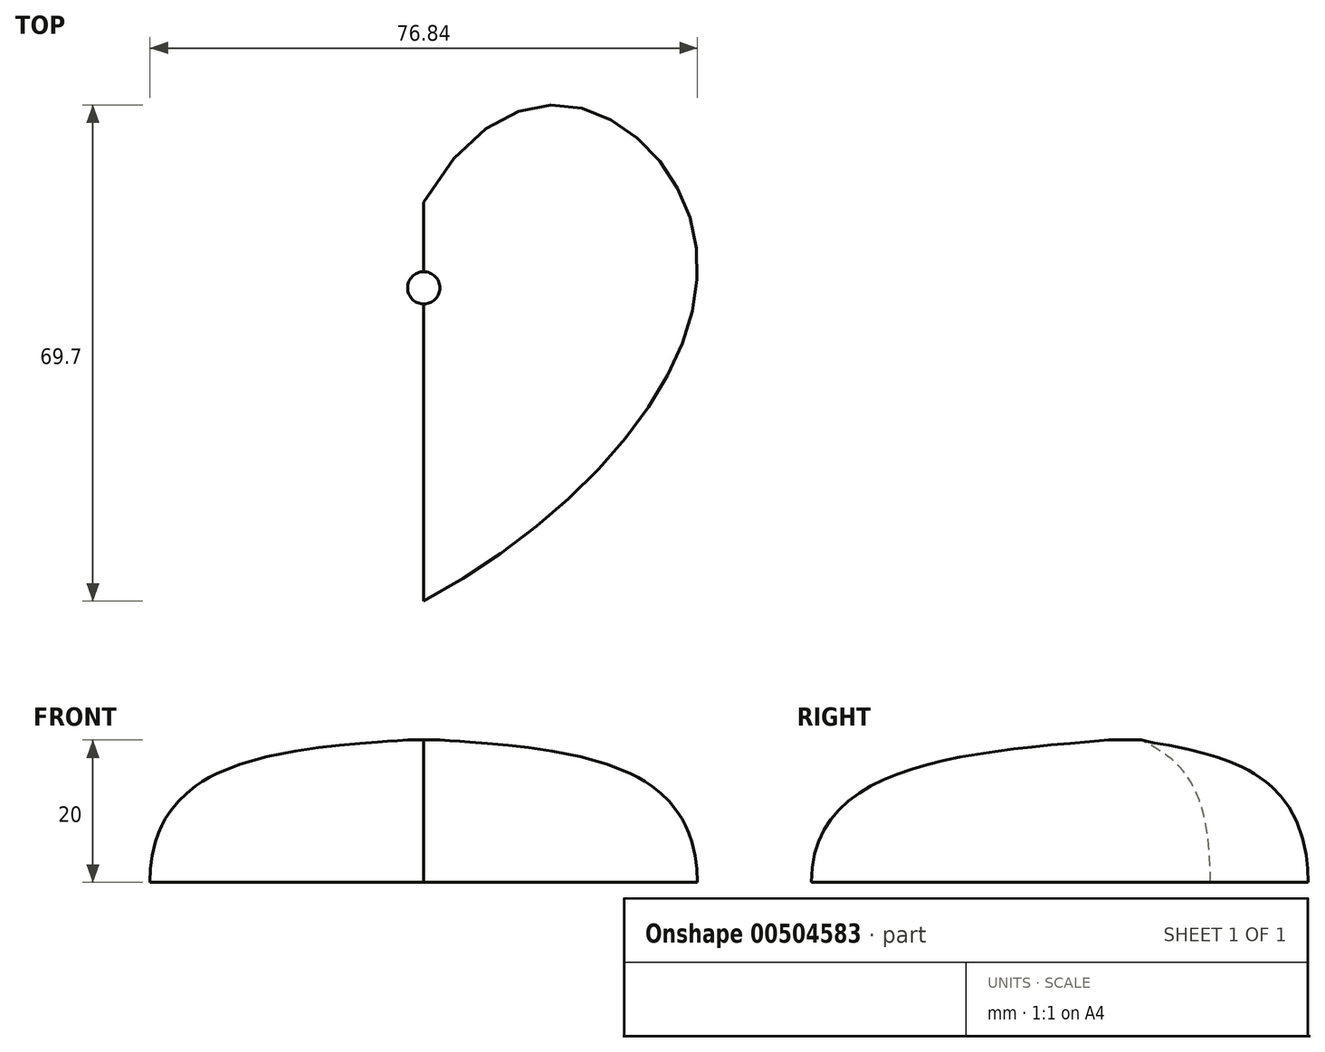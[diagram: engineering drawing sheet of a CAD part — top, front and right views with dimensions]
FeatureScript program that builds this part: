
annotation { "Feature Type Name" : "Feature", "Feature Type Description" : "" }
export const myFeature = defineFeature(function(context is Context, id is Id, definition is map)
    precondition{}
    {
        {
            var Q0;
            Q0=qCreatedBy(makeId("Top.planeOp"),FACE);
            var sketch = newSketch(context, id + "F0", { "sketchPlane" : qUnion([Q0])});
            skFitSpline(sketch, "E0", {"points": [v(0, -25) * mm, v(37.2, -26.59) * mm, v(0, -81) * mm], "startDerivative": vector(94.86, 165.83) * mm, "endDerivative": vector(-129.77, -70.47) * mm});
            skFitSpline(sketch, "E1.MirrorCS", {"points": [v(0, -25) * mm, v(-37.2, -26.59) * mm, v(0, -81) * mm], "startDerivative": vector(-94.86, 165.83) * mm, "endDerivative": vector(129.77, -70.47) * mm});
            skSolve(sketch);
        }
        {
            var Q0;
            Q0=qCreatedBy(makeId("Top.planeOp"),FACE);
            cPlane(context, id + "F1", {"entities" : qUnion([Q0]), "cplaneType" : CPlaneType.OFFSET, "offset" : 20 * mm, "width" : 150 * mm, "height" : 150 * mm});
        }
        {
            var Q0;
            Q0=qCreatedBy(id+"F1.planeOp",FACE);
            var sketch = newSketch(context, id + "F2", { "sketchPlane" : qUnion([Q0])});
            skCircle(sketch, "E2", {"center": v(0, -37) * mm, "radius": 2.27 * mm});
            skSolve(sketch);
        }
        {
            var Q0;
            Q0=makeQuery(id+"F0.imprint","IMPRINT",FACE,{"disambiguationData":[TD([[makeQuery(id+"F0.imprint","IMPRINT",EDGE,{"derivedFrom":sQuery(id+"F0.wireOp",EDGE,"E0")}),-1.0]])]});
            var Q1;
            Q1=makeQuery(id+"F2.imprint","IMPRINT",FACE,{"disambiguationData":[TD([[makeQuery(id+"F2.imprint","IMPRINT",EDGE,{"derivedFrom":sQuery(id+"F2.wireOp",EDGE,"E2")}),1.0]])]});
            loft(context, id + "F3", {"startCondition" : LoftEndDerivativeType.NORMAL_TO_PROFILE, "startMagnitude" : 2.2, "endCondition" : LoftEndDerivativeType.NORMAL_TO_PROFILE, "endMagnitude" : 0, "sheetProfilesArray" : [{ "sheetProfileEntities" : qUnion([Q0]) }, { "sheetProfileEntities" : qUnion([Q1]) }]});
        }
    });
